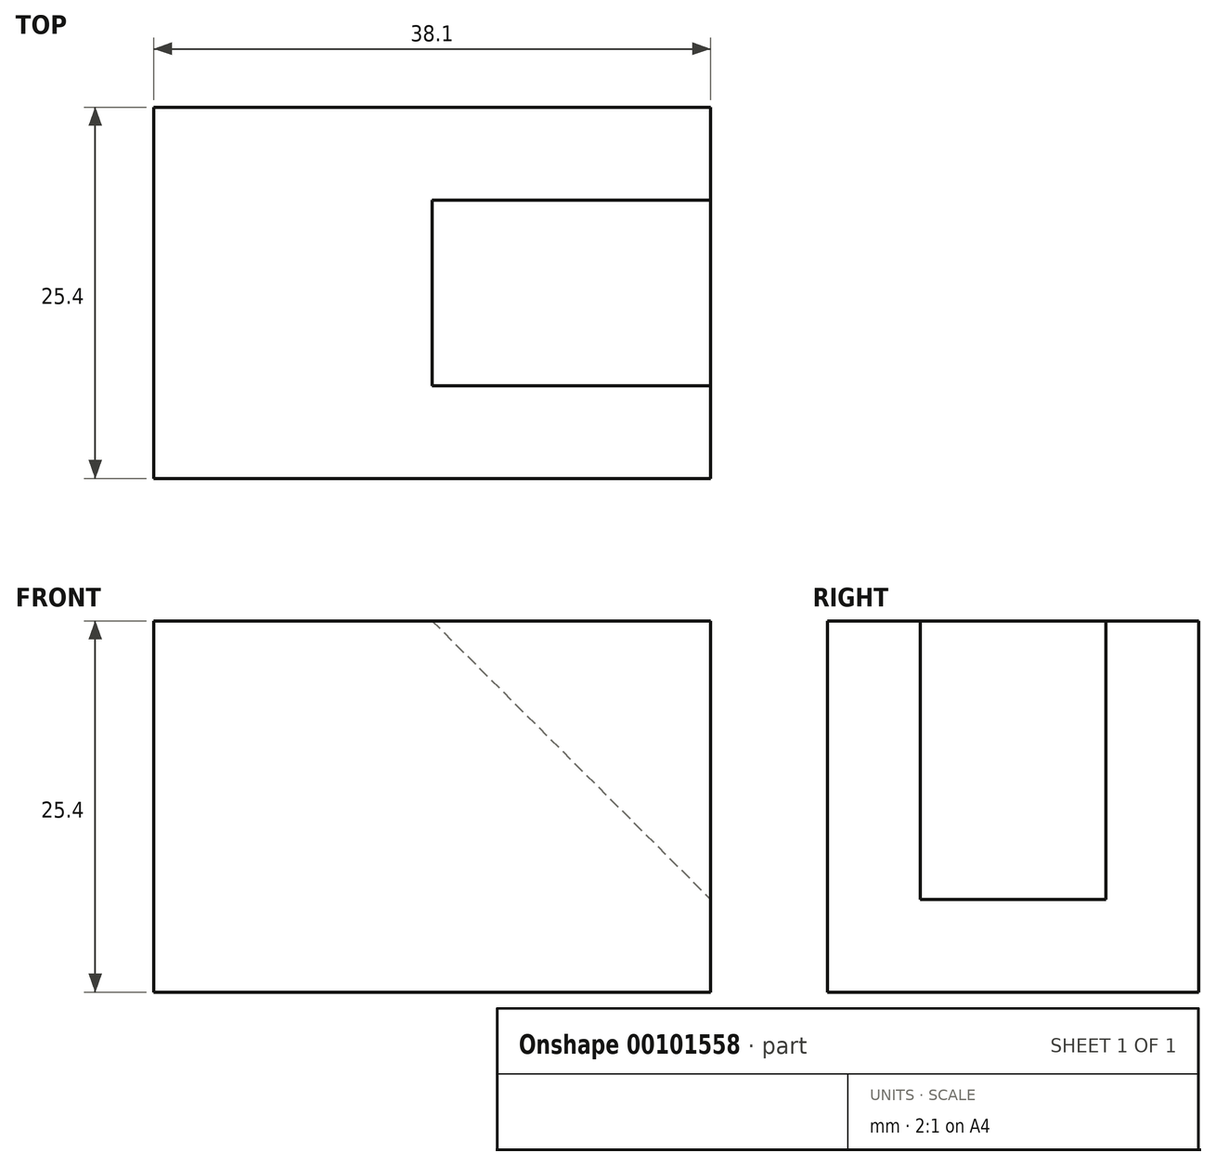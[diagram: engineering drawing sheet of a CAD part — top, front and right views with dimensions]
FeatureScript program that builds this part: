
annotation { "Feature Type Name" : "Feature", "Feature Type Description" : "" }
export const myFeature = defineFeature(function(context is Context, id is Id, definition is map)
    precondition{}
    {
        {
            var Q0;
            Q0=qCreatedBy(makeId("Front.planeOp"),FACE);
            var sketch = newSketch(context, id + "F0", { "sketchPlane" : qUnion([Q0])});
            skLineSegment(sketch, "E0.bottom", {"start": v(0, 0) * mm, "end": v(-38.1, 0) * mm});
            skLineSegment(sketch, "E0.top", {"start": v(0, -25.4) * mm, "end": v(-38.1, -25.4) * mm});
            skLineSegment(sketch, "E0.left", {"start": v(0, 0) * mm, "end": v(0, -25.4) * mm});
            skLineSegment(sketch, "E0.right", {"start": v(-38.1, 0) * mm, "end": v(-38.1, -25.4) * mm});
            skSolve(sketch);
        }
        {
            var Q0;
            Q0=makeQuery(id+"F0.imprint","IMPRINT",FACE,{"disambiguationData":[TD([[makeQuery(id+"F0.imprint","IMPRINT",EDGE,{"derivedFrom":sQuery(id+"F0.wireOp",EDGE,"E0.bottom")}),1.0]])]});
            extrude(context, id + "F1", {"entities" : qUnion([Q0]), "endBound" : BoundingType.SYMMETRIC, "oppositeDirection" : true, "depth" : 25.4 * mm});
        }
        {
            var Q0;
            Q0=qCreatedBy(makeId("Front.planeOp"),FACE);
            var sketch = newSketch(context, id + "F2", { "sketchPlane" : qUnion([Q0])});
            skLineSegment(sketch, "E1", {"start": v(0, 0) * mm, "end": v(-19.05, 0) * mm});
            skLineSegment(sketch, "E2", {"start": v(-19.05, 0) * mm, "end": v(0, -19.05) * mm});
            skLineSegment(sketch, "E3", {"start": v(0, -19.05) * mm, "end": v(0, 0) * mm});
            skSolve(sketch);
        }
        {
            var Q0;
            Q0 = qSketchRegion(id + "F2", true);
            extrude(context, id + "F3", {"entities" : qUnion([Q0]), "operationType" : NewBodyOperationType.REMOVE, "endBound" : BoundingType.SYMMETRIC, "oppositeDirection" : true, "depth" : 12.7 * mm});
        }
    });
